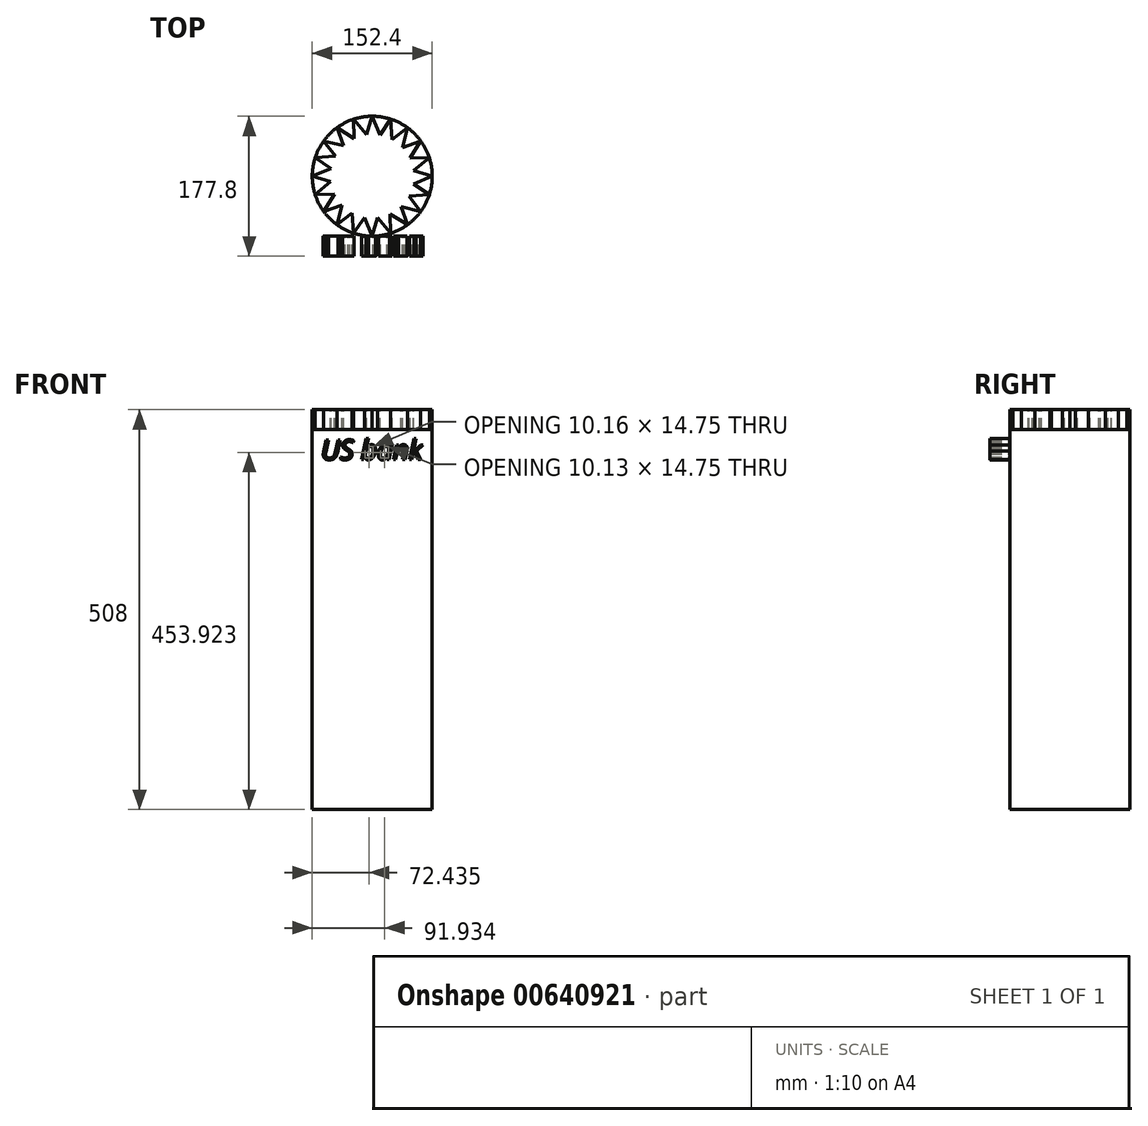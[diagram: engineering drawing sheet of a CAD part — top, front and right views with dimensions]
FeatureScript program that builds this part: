
annotation { "Feature Type Name" : "Feature", "Feature Type Description" : "" }
export const myFeature = defineFeature(function(context is Context, id is Id, definition is map)
    precondition{}
    {
        {
            var Q0;
            Q0=qCreatedBy(makeId("Top.planeOp"),FACE);
            var sketch = newSketch(context, id + "F0", { "sketchPlane" : qUnion([Q0])});
            skCircle(sketch, "E0", {"center": v(0, 0) * mm, "radius": 76.2 * mm});
            skSolve(sketch);
        }
        {
            var Q0;
            Q0=makeQuery(id+"F0.imprint","IMPRINT",FACE,{"disambiguationData":[TD([[makeQuery(id+"F0.imprint","IMPRINT",EDGE,{"derivedFrom":sQuery(id+"F0.wireOp",EDGE,"E0")}),1.0]])]});
            extrude(context, id + "F1", {"entities" : qUnion([Q0]), "depth" : 508 * mm, "offsetDistance" : 25.4 * mm});
        }
        {
            var Q0;
            Q0=makeQuery(id+"F1.opExtrude","CAP_FACE",FACE,{"disambiguationData":[OSD([sQuery(id+"F0.wireOp",EDGE,"E0")])],"isStart":false});
            var sketch = newSketch(context, id + "F2", { "sketchPlane" : qUnion([Q0])});
            skCircle(sketch, "E1", {"center": v(0, 0) * mm, "radius": 50.8 * mm});
            skLineSegment(sketch, "E2", {"start": v(-7.7, 50.21) * mm, "end": v(0, 76.2) * mm});
            skLineSegment(sketch, "E3", {"start": v(0, 76.2) * mm, "end": v(10.79, 49.64) * mm});
            skLineSegment(sketch, "E4.1.0", {"start": v(-22.83, 45.38) * mm, "end": v(-23.55, 72.47) * mm});
            skLineSegment(sketch, "E4.1.1", {"start": v(-23.55, 72.47) * mm, "end": v(-5.08, 50.55) * mm});
            skLineSegment(sketch, "E4.2.0", {"start": v(-35.74, 36.1) * mm, "end": v(-44.79, 61.65) * mm});
            skLineSegment(sketch, "E4.2.1", {"start": v(-44.79, 61.65) * mm, "end": v(-20.45, 46.5) * mm});
            skLineSegment(sketch, "E4.3.0", {"start": v(-45.15, 23.3) * mm, "end": v(-61.65, 44.79) * mm});
            skLineSegment(sketch, "E4.3.1", {"start": v(-61.65, 44.79) * mm, "end": v(-33.82, 37.9) * mm});
            skLineSegment(sketch, "E4.4.0", {"start": v(-50.13, 8.2) * mm, "end": v(-72.47, 23.55) * mm});
            skLineSegment(sketch, "E4.4.1", {"start": v(-72.47, 23.55) * mm, "end": v(-43.88, 25.6) * mm});
            skLineSegment(sketch, "E4.5.0", {"start": v(-50.21, -7.7) * mm, "end": v(-76.2, 0) * mm});
            skLineSegment(sketch, "E4.5.1", {"start": v(-76.2, 0) * mm, "end": v(-49.64, 10.79) * mm});
            skLineSegment(sketch, "E4.6.0", {"start": v(-45.38, -22.83) * mm, "end": v(-72.47, -23.55) * mm});
            skLineSegment(sketch, "E4.6.1", {"start": v(-72.47, -23.55) * mm, "end": v(-50.55, -5.08) * mm});
            skLineSegment(sketch, "E4.7.0", {"start": v(-36.1, -35.74) * mm, "end": v(-61.65, -44.79) * mm});
            skLineSegment(sketch, "E4.7.1", {"start": v(-61.65, -44.79) * mm, "end": v(-46.5, -20.45) * mm});
            skLineSegment(sketch, "E4.8.0", {"start": v(-23.3, -45.15) * mm, "end": v(-44.79, -61.65) * mm});
            skLineSegment(sketch, "E4.8.1", {"start": v(-44.79, -61.65) * mm, "end": v(-37.9, -33.82) * mm});
            skLineSegment(sketch, "E4.9.0", {"start": v(-8.2, -50.13) * mm, "end": v(-23.55, -72.47) * mm});
            skLineSegment(sketch, "E4.9.1", {"start": v(-23.55, -72.47) * mm, "end": v(-25.6, -43.88) * mm});
            skLineSegment(sketch, "E4.10.0", {"start": v(7.7, -50.21) * mm, "end": v(0, -76.2) * mm});
            skLineSegment(sketch, "E4.10.1", {"start": v(0, -76.2) * mm, "end": v(-10.79, -49.64) * mm});
            skLineSegment(sketch, "E4.11.0", {"start": v(22.83, -45.38) * mm, "end": v(23.55, -72.47) * mm});
            skLineSegment(sketch, "E4.11.1", {"start": v(23.55, -72.47) * mm, "end": v(5.08, -50.55) * mm});
            skLineSegment(sketch, "E4.12.0", {"start": v(35.74, -36.1) * mm, "end": v(44.79, -61.65) * mm});
            skLineSegment(sketch, "E4.12.1", {"start": v(44.79, -61.65) * mm, "end": v(20.45, -46.5) * mm});
            skLineSegment(sketch, "E4.13.0", {"start": v(45.15, -23.3) * mm, "end": v(61.65, -44.79) * mm});
            skLineSegment(sketch, "E4.13.1", {"start": v(61.65, -44.79) * mm, "end": v(33.82, -37.9) * mm});
            skLineSegment(sketch, "E4.14.0", {"start": v(50.13, -8.2) * mm, "end": v(72.47, -23.55) * mm});
            skLineSegment(sketch, "E4.14.1", {"start": v(72.47, -23.55) * mm, "end": v(43.88, -25.6) * mm});
            skLineSegment(sketch, "E4.15.0", {"start": v(50.21, 7.7) * mm, "end": v(76.2, 0) * mm});
            skLineSegment(sketch, "E4.15.1", {"start": v(76.2, 0) * mm, "end": v(49.64, -10.79) * mm});
            skLineSegment(sketch, "E4.16.0", {"start": v(45.38, 22.83) * mm, "end": v(72.47, 23.55) * mm});
            skLineSegment(sketch, "E4.16.1", {"start": v(72.47, 23.55) * mm, "end": v(50.55, 5.08) * mm});
            skLineSegment(sketch, "E4.17.0", {"start": v(36.1, 35.74) * mm, "end": v(61.65, 44.79) * mm});
            skLineSegment(sketch, "E4.17.1", {"start": v(61.65, 44.79) * mm, "end": v(46.5, 20.45) * mm});
            skLineSegment(sketch, "E4.18.0", {"start": v(23.3, 45.15) * mm, "end": v(44.79, 61.65) * mm});
            skLineSegment(sketch, "E4.18.1", {"start": v(44.79, 61.65) * mm, "end": v(37.9, 33.82) * mm});
            skLineSegment(sketch, "E4.19.0", {"start": v(8.2, 50.13) * mm, "end": v(23.55, 72.47) * mm});
            skLineSegment(sketch, "E4.19.1", {"start": v(23.55, 72.47) * mm, "end": v(25.6, 43.88) * mm});
            skSolve(sketch);
        }
        {
            var Q0;
            {var subQ0=sQuery(id+"F2.wireOp",EDGE,"E4.1.0");var subQ3=sQuery(id+"F2.wireOp",EDGE,"E4.2.1");var subQ4=makeQuery(id+"F2.imprint","INTERSECT",VERTEX,{"derivedFrom":[subQ0,subQ3]});Q0=makeQuery(id+"F2.imprint","IMPRINT",FACE,{"disambiguationData":[TD([[makeQuery(id+"F2.imprint","IMPRINT",EDGE,{"disambiguationData":[TD([[subQ4,-1.0]])],"derivedFrom":subQ0}),1.0]])]});}
            var Q1;
            {var subQ0=sQuery(id+"F2.wireOp",EDGE,"E2");var subQ3=sQuery(id+"F2.wireOp",EDGE,"E4.1.1");var subQ4=makeQuery(id+"F2.imprint","INTERSECT",VERTEX,{"derivedFrom":[subQ0,subQ3]});Q1=makeQuery(id+"F2.imprint","IMPRINT",FACE,{"disambiguationData":[TD([[makeQuery(id+"F2.imprint","IMPRINT",EDGE,{"disambiguationData":[TD([[subQ4,-1.0]])],"derivedFrom":subQ0}),1.0]])]});}
            var Q2;
            {var subQ0=sQuery(id+"F2.wireOp",EDGE,"E3");var subQ3=sQuery(id+"F2.wireOp",EDGE,"E4.19.0");var subQ4=makeQuery(id+"F2.imprint","INTERSECT",VERTEX,{"derivedFrom":[subQ0,subQ3]});Q2=makeQuery(id+"F2.imprint","IMPRINT",FACE,{"disambiguationData":[TD([[makeQuery(id+"F2.imprint","IMPRINT",EDGE,{"disambiguationData":[TD([[subQ4,1.0]])],"derivedFrom":subQ0}),1.0]])]});}
            var Q3;
            {var subQ0=sQuery(id+"F2.wireOp",EDGE,"E4.18.0");var subQ3=sQuery(id+"F2.wireOp",EDGE,"E4.19.1");var subQ4=makeQuery(id+"F2.imprint","INTERSECT",VERTEX,{"derivedFrom":[subQ0,subQ3]});Q3=makeQuery(id+"F2.imprint","IMPRINT",FACE,{"disambiguationData":[TD([[makeQuery(id+"F2.imprint","IMPRINT",EDGE,{"disambiguationData":[TD([[subQ4,-1.0]])],"derivedFrom":subQ0}),1.0]])]});}
            var Q4;
            {var subQ0=sQuery(id+"F2.wireOp",EDGE,"E4.17.0");var subQ3=sQuery(id+"F2.wireOp",EDGE,"E4.18.1");var subQ4=makeQuery(id+"F2.imprint","INTERSECT",VERTEX,{"derivedFrom":[subQ0,subQ3]});Q4=makeQuery(id+"F2.imprint","IMPRINT",FACE,{"disambiguationData":[TD([[makeQuery(id+"F2.imprint","IMPRINT",EDGE,{"disambiguationData":[TD([[subQ4,-1.0]])],"derivedFrom":subQ0}),1.0]])]});}
            var Q5;
            {var subQ0=sQuery(id+"F2.wireOp",EDGE,"E4.16.0");var subQ3=sQuery(id+"F2.wireOp",EDGE,"E4.17.1");var subQ4=makeQuery(id+"F2.imprint","INTERSECT",VERTEX,{"derivedFrom":[subQ0,subQ3]});Q5=makeQuery(id+"F2.imprint","IMPRINT",FACE,{"disambiguationData":[TD([[makeQuery(id+"F2.imprint","IMPRINT",EDGE,{"disambiguationData":[TD([[subQ4,-1.0]])],"derivedFrom":subQ0}),1.0]])]});}
            var Q6;
            {var subQ0=sQuery(id+"F2.wireOp",EDGE,"E4.15.0");var subQ3=sQuery(id+"F2.wireOp",EDGE,"E4.16.1");var subQ4=makeQuery(id+"F2.imprint","INTERSECT",VERTEX,{"derivedFrom":[subQ0,subQ3]});Q6=makeQuery(id+"F2.imprint","IMPRINT",FACE,{"disambiguationData":[TD([[makeQuery(id+"F2.imprint","IMPRINT",EDGE,{"disambiguationData":[TD([[subQ4,-1.0]])],"derivedFrom":subQ0}),1.0]])]});}
            var Q7;
            {var subQ0=sQuery(id+"F2.wireOp",EDGE,"E4.14.0");var subQ3=sQuery(id+"F2.wireOp",EDGE,"E4.15.1");var subQ4=makeQuery(id+"F2.imprint","INTERSECT",VERTEX,{"derivedFrom":[subQ0,subQ3]});Q7=makeQuery(id+"F2.imprint","IMPRINT",FACE,{"disambiguationData":[TD([[makeQuery(id+"F2.imprint","IMPRINT",EDGE,{"disambiguationData":[TD([[subQ4,-1.0]])],"derivedFrom":subQ0}),1.0]])]});}
            var Q8;
            {var subQ0=sQuery(id+"F2.wireOp",EDGE,"E4.13.0");var subQ3=sQuery(id+"F2.wireOp",EDGE,"E4.14.1");var subQ4=makeQuery(id+"F2.imprint","INTERSECT",VERTEX,{"derivedFrom":[subQ0,subQ3]});Q8=makeQuery(id+"F2.imprint","IMPRINT",FACE,{"disambiguationData":[TD([[makeQuery(id+"F2.imprint","IMPRINT",EDGE,{"disambiguationData":[TD([[subQ4,-1.0]])],"derivedFrom":subQ0}),1.0]])]});}
            var Q9;
            {var subQ0=sQuery(id+"F2.wireOp",EDGE,"E4.12.0");var subQ3=sQuery(id+"F2.wireOp",EDGE,"E4.13.1");var subQ4=makeQuery(id+"F2.imprint","INTERSECT",VERTEX,{"derivedFrom":[subQ0,subQ3]});Q9=makeQuery(id+"F2.imprint","IMPRINT",FACE,{"disambiguationData":[TD([[makeQuery(id+"F2.imprint","IMPRINT",EDGE,{"disambiguationData":[TD([[subQ4,-1.0]])],"derivedFrom":subQ0}),1.0]])]});}
            var Q10;
            {var subQ0=sQuery(id+"F2.wireOp",EDGE,"E4.11.0");var subQ3=sQuery(id+"F2.wireOp",EDGE,"E4.12.1");var subQ4=makeQuery(id+"F2.imprint","INTERSECT",VERTEX,{"derivedFrom":[subQ0,subQ3]});Q10=makeQuery(id+"F2.imprint","IMPRINT",FACE,{"disambiguationData":[TD([[makeQuery(id+"F2.imprint","IMPRINT",EDGE,{"disambiguationData":[TD([[subQ4,-1.0]])],"derivedFrom":subQ0}),1.0]])]});}
            var Q11;
            {var subQ0=sQuery(id+"F2.wireOp",EDGE,"E4.10.0");var subQ3=sQuery(id+"F2.wireOp",EDGE,"E4.11.1");var subQ4=makeQuery(id+"F2.imprint","INTERSECT",VERTEX,{"derivedFrom":[subQ0,subQ3]});Q11=makeQuery(id+"F2.imprint","IMPRINT",FACE,{"disambiguationData":[TD([[makeQuery(id+"F2.imprint","IMPRINT",EDGE,{"disambiguationData":[TD([[subQ4,-1.0]])],"derivedFrom":subQ0}),1.0]])]});}
            var Q12;
            {var subQ0=sQuery(id+"F2.wireOp",EDGE,"E4.9.0");var subQ3=sQuery(id+"F2.wireOp",EDGE,"E4.10.1");var subQ4=makeQuery(id+"F2.imprint","INTERSECT",VERTEX,{"derivedFrom":[subQ0,subQ3]});Q12=makeQuery(id+"F2.imprint","IMPRINT",FACE,{"disambiguationData":[TD([[makeQuery(id+"F2.imprint","IMPRINT",EDGE,{"disambiguationData":[TD([[subQ4,-1.0]])],"derivedFrom":subQ0}),1.0]])]});}
            var Q13;
            {var subQ0=sQuery(id+"F2.wireOp",EDGE,"E4.8.0");var subQ3=sQuery(id+"F2.wireOp",EDGE,"E4.9.1");var subQ4=makeQuery(id+"F2.imprint","INTERSECT",VERTEX,{"derivedFrom":[subQ0,subQ3]});Q13=makeQuery(id+"F2.imprint","IMPRINT",FACE,{"disambiguationData":[TD([[makeQuery(id+"F2.imprint","IMPRINT",EDGE,{"disambiguationData":[TD([[subQ4,-1.0]])],"derivedFrom":subQ0}),1.0]])]});}
            var Q14;
            {var subQ0=sQuery(id+"F2.wireOp",EDGE,"E4.7.0");var subQ3=sQuery(id+"F2.wireOp",EDGE,"E4.8.1");var subQ4=makeQuery(id+"F2.imprint","INTERSECT",VERTEX,{"derivedFrom":[subQ0,subQ3]});Q14=makeQuery(id+"F2.imprint","IMPRINT",FACE,{"disambiguationData":[TD([[makeQuery(id+"F2.imprint","IMPRINT",EDGE,{"disambiguationData":[TD([[subQ4,-1.0]])],"derivedFrom":subQ0}),1.0]])]});}
            var Q15;
            {var subQ0=sQuery(id+"F2.wireOp",EDGE,"E4.6.0");var subQ3=sQuery(id+"F2.wireOp",EDGE,"E4.7.1");var subQ4=makeQuery(id+"F2.imprint","INTERSECT",VERTEX,{"derivedFrom":[subQ0,subQ3]});Q15=makeQuery(id+"F2.imprint","IMPRINT",FACE,{"disambiguationData":[TD([[makeQuery(id+"F2.imprint","IMPRINT",EDGE,{"disambiguationData":[TD([[subQ4,-1.0]])],"derivedFrom":subQ0}),1.0]])]});}
            var Q16;
            {var subQ0=sQuery(id+"F2.wireOp",EDGE,"E4.5.0");var subQ3=sQuery(id+"F2.wireOp",EDGE,"E4.6.1");var subQ4=makeQuery(id+"F2.imprint","INTERSECT",VERTEX,{"derivedFrom":[subQ0,subQ3]});Q16=makeQuery(id+"F2.imprint","IMPRINT",FACE,{"disambiguationData":[TD([[makeQuery(id+"F2.imprint","IMPRINT",EDGE,{"disambiguationData":[TD([[subQ4,-1.0]])],"derivedFrom":subQ0}),1.0]])]});}
            var Q17;
            {var subQ0=sQuery(id+"F2.wireOp",EDGE,"E4.4.0");var subQ3=sQuery(id+"F2.wireOp",EDGE,"E4.5.1");var subQ4=makeQuery(id+"F2.imprint","INTERSECT",VERTEX,{"derivedFrom":[subQ0,subQ3]});Q17=makeQuery(id+"F2.imprint","IMPRINT",FACE,{"disambiguationData":[TD([[makeQuery(id+"F2.imprint","IMPRINT",EDGE,{"disambiguationData":[TD([[subQ4,-1.0]])],"derivedFrom":subQ0}),1.0]])]});}
            var Q18;
            {var subQ0=sQuery(id+"F2.wireOp",EDGE,"E4.3.0");var subQ3=sQuery(id+"F2.wireOp",EDGE,"E4.4.1");var subQ4=makeQuery(id+"F2.imprint","INTERSECT",VERTEX,{"derivedFrom":[subQ0,subQ3]});Q18=makeQuery(id+"F2.imprint","IMPRINT",FACE,{"disambiguationData":[TD([[makeQuery(id+"F2.imprint","IMPRINT",EDGE,{"disambiguationData":[TD([[subQ4,-1.0]])],"derivedFrom":subQ0}),1.0]])]});}
            var Q19;
            {var subQ0=sQuery(id+"F2.wireOp",EDGE,"E4.2.0");var subQ3=sQuery(id+"F2.wireOp",EDGE,"E4.3.1");var subQ4=makeQuery(id+"F2.imprint","INTERSECT",VERTEX,{"derivedFrom":[subQ0,subQ3]});Q19=makeQuery(id+"F2.imprint","IMPRINT",FACE,{"disambiguationData":[TD([[makeQuery(id+"F2.imprint","IMPRINT",EDGE,{"disambiguationData":[TD([[subQ4,-1.0]])],"derivedFrom":subQ0}),1.0]])]});}
            extrude(context, id + "F3", {"entities" : qUnion([Q0, Q1, Q2, Q3, Q4, Q5, Q6, Q7, Q8, Q9, Q10, Q11, Q12, Q13, Q14, Q15, Q16, Q17, Q18, Q19]), "operationType" : NewBodyOperationType.REMOVE, "oppositeDirection" : true, "depth" : 25.4 * mm, "offsetDistance" : 25.4 * mm});
        }
        {
            var Q0;
            Q0=qCreatedBy(makeId("Front.planeOp"),FACE);
            cPlane(context, id + "F4", {"entities" : qUnion([Q0]), "cplaneType" : CPlaneType.OFFSET, "offset" : 76.2 * mm, "width" : 152.4 * mm, "height" : 152.4 * mm});
        }
        {
            var Q0;
            Q0=qCreatedBy(id+"F4.planeOp",FACE);
            var sketch = newSketch(context, id + "F5", { "sketchPlane" : qUnion([Q0])});
            skText(sketch, "E5", { "text": "US bank", "fontName": "OpenSans-Italic.ttf"});
            const initialGuessF5  = {"E5": [-0.06506, 0.4445, 1, 0, 0.0254]};
            skSetInitialGuess(sketch, initialGuessF5);
            skSolve(sketch);
        }
        {
            var Q0;
            Q0 = qSketchRegion(id + "F5", true);
            extrude(context, id + "F6", {"entities" : qUnion([Q0]), "operationType" : NewBodyOperationType.ADD, "depth" : 25.4 * mm, "offsetDistance" : 25.4 * mm});
        }
    });
